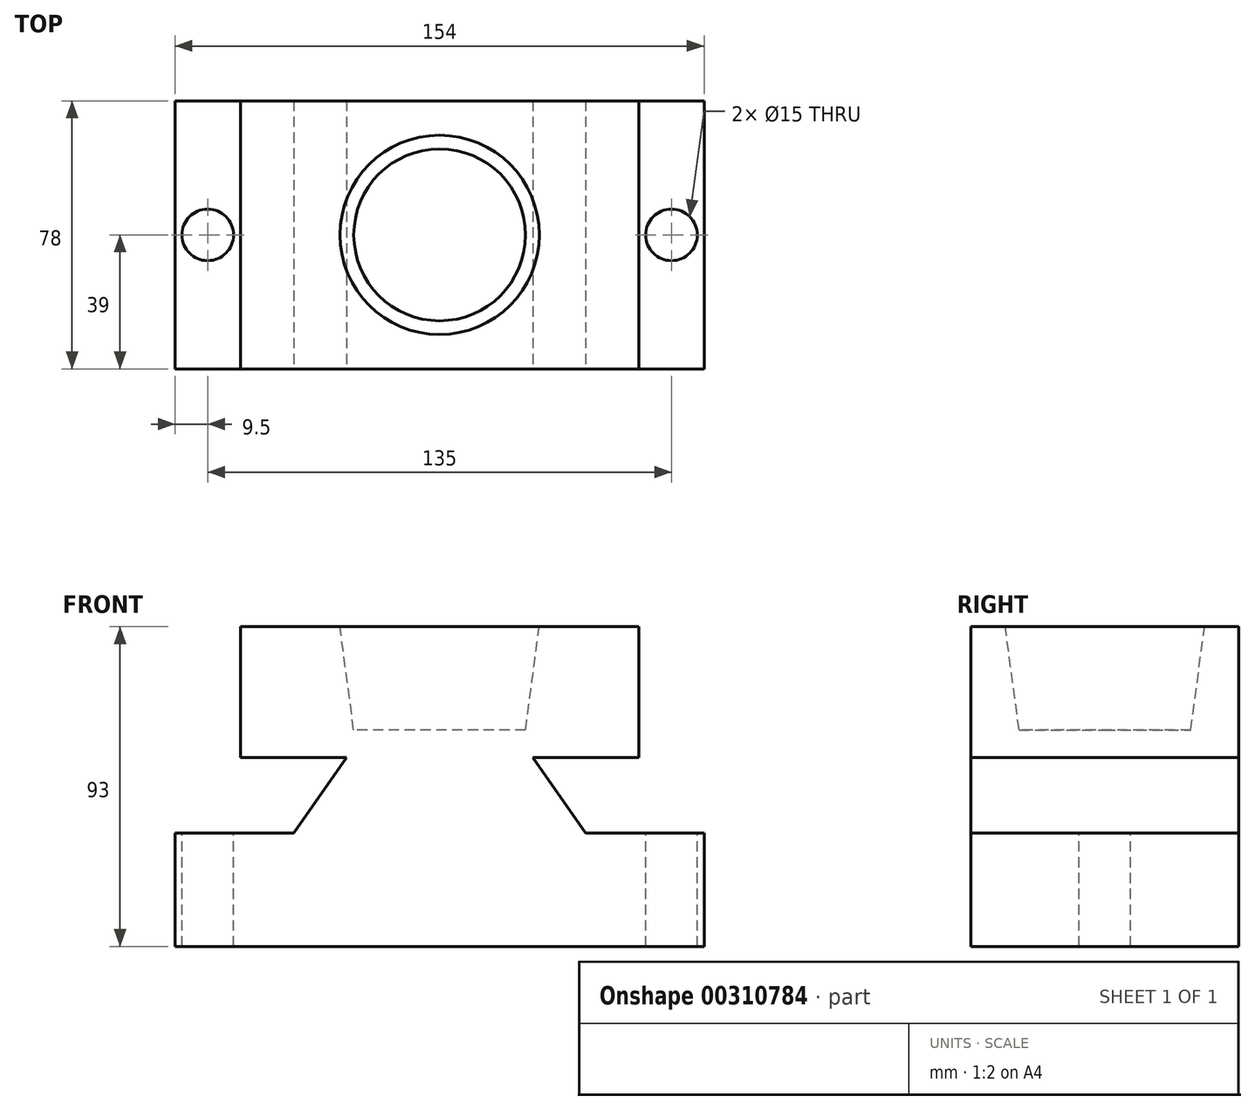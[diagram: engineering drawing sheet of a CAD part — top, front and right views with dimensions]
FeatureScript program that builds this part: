
annotation { "Feature Type Name" : "Feature", "Feature Type Description" : "" }
export const myFeature = defineFeature(function(context is Context, id is Id, definition is map)
    precondition{}
    {
        {
            var Q0;
            Q0=qCreatedBy(makeId("Top.planeOp"),FACE);
            var sketch = newSketch(context, id + "F0", { "sketchPlane" : qUnion([Q0])});
            skLineSegment(sketch, "E0.bottom", {"start": v(-77, 39) * mm, "end": v(77, 39) * mm});
            skLineSegment(sketch, "E0.top", {"start": v(-77, -39) * mm, "end": v(77, -39) * mm});
            skLineSegment(sketch, "E0.left", {"start": v(-77, 39) * mm, "end": v(-77, -39) * mm});
            skLineSegment(sketch, "E0.right", {"start": v(77, 39) * mm, "end": v(77, -39) * mm});
            skPoint(sketch, "E0.middle", {"position": v(0, 0) * mm});
            skSolve(sketch);
        }
        {
            var Q0;
            Q0=makeQuery(id+"F0.imprint","IMPRINT",FACE,{"disambiguationData":[TD([[makeQuery(id+"F0.imprint","IMPRINT",EDGE,{"derivedFrom":sQuery(id+"F0.wireOp",EDGE,"E0.bottom")}),-1.0]])]});
            extrude(context, id + "F1", {"entities" : qUnion([Q0]), "endBound" : BoundingType.SYMMETRIC, "depth" : 93 * mm});
        }
        {
            var Q0;
            Q0=makeQuery(id+"F1.opExtrude","SWEPT_FACE",FACE,{"disambiguationData":[OSD([sQuery(id+"F0.wireOp",EDGE,"E0.top")])]});
            var sketch = newSketch(context, id + "F2", { "sketchPlane" : qUnion([Q0])});
            skLineSegment(sketch, "E1", {"start": v(-77, -13.5) * mm, "end": v(-42.5, -13.5) * mm});
            skLineSegment(sketch, "E2", {"start": v(-42.5, -13.5) * mm, "end": v(-27.1, 8.5) * mm});
            skLineSegment(sketch, "E3", {"start": v(-27.1, 8.5) * mm, "end": v(-58, 8.5) * mm});
            skLineSegment(sketch, "E4", {"start": v(-58, 8.5) * mm, "end": v(-58, 46.5) * mm});
            skLineSegment(sketch, "E5", {"start": v(-58, 46.5) * mm, "end": v(58, 46.5) * mm});
            skLineSegment(sketch, "E6", {"start": v(58, 46.5) * mm, "end": v(58, 8.5) * mm});
            skLineSegment(sketch, "E7", {"start": v(58, 8.5) * mm, "end": v(27.1, 8.5) * mm});
            skLineSegment(sketch, "E8", {"start": v(27.1, 8.5) * mm, "end": v(42.5, -13.5) * mm});
            skLineSegment(sketch, "E9", {"start": v(42.5, -13.5) * mm, "end": v(77, -13.5) * mm});
            skSolve(sketch);
        }
        {
            var Q0;
            {var subQ5=sQuery(id+"F2.wireOp",EDGE,"E1");Q0=makeQuery(id+"F2.imprint","IMPRINT",FACE,{"disambiguationData":[TD([[makeQuery(id+"F2.imprint","IMPRINT",EDGE,{"derivedFrom":subQ5}),1.0]])]});}
            var Q1;
            {var subQ1=sQuery(id+"F2.wireOp",EDGE,"E6");Q1=makeQuery(id+"F2.imprint","IMPRINT",FACE,{"disambiguationData":[TD([[makeQuery(id+"F2.imprint","IMPRINT",EDGE,{"derivedFrom":subQ1}),1.0]])]});}
            extrude(context, id + "F3", {"entities" : qUnion([Q0, Q1]), "operationType" : NewBodyOperationType.REMOVE, "oppositeDirection" : true, "depth" : 80 * mm});
        }
        {
            var Q0;
            Q0=makeQuery(id+"F3.boolean.opBoolean","COPY",FACE,{"derivedFrom":makeQuery(id+"F3.opExtrude","SWEPT_FACE",FACE,{"disambiguationData":[OSD([sQuery(id+"F2.wireOp",EDGE,"E1")])]})});
            var sketch = newSketch(context, id + "F4", { "sketchPlane" : qUnion([Q0])});
            skCircle(sketch, "E10", {"center": v(-67.5, 0) * mm, "radius": 9.5 * mm});
            skCircle(sketch, "E11", {"center": v(-67.5, 0) * mm, "radius": 7.5 * mm});
            skSolve(sketch);
        }
        {
            var Q0;
            Q0=makeQuery(id+"F4.imprint","IMPRINT",FACE,{"disambiguationData":[TD([[makeQuery(id+"F4.imprint","IMPRINT",EDGE,{"derivedFrom":sQuery(id+"F4.wireOp",EDGE,"E11")}),1.0]])]});
            extrude(context, id + "F5", {"entities" : qUnion([Q0]), "operationType" : NewBodyOperationType.REMOVE, "oppositeDirection" : true, "depth" : 50 * mm});
        }
        {
            var Q0;
            Q0=makeQuery(id+"F1.opExtrude","CAP_FACE",FACE,{"disambiguationData":[OSD([sQuery(id+"F0.wireOp",EDGE,"E0.bottom"),sQuery(id+"F0.wireOp",EDGE,"E0.top"),sQuery(id+"F0.wireOp",EDGE,"E0.left"),sQuery(id+"F0.wireOp",EDGE,"E0.right")])],"isStart":false});
            var sketch = newSketch(context, id + "F6", { "sketchPlane" : qUnion([Q0])});
            skCircle(sketch, "E12", {"center": v(0, 0) * mm, "radius": 29 * mm});
            skCircle(sketch, "E13", {"center": v(0, 0) * mm, "radius": 31 * mm});
            skSolve(sketch);
        }
        {
            var Q0;
            Q0=makeQuery(id+"F6.imprint","IMPRINT",FACE,{"disambiguationData":[TD([[makeQuery(id+"F6.imprint","IMPRINT",EDGE,{"derivedFrom":sQuery(id+"F6.wireOp",EDGE,"E12")}),1.0]])]});
            extrude(context, id + "F7", {"entities" : qUnion([Q0]), "operationType" : NewBodyOperationType.REMOVE, "oppositeDirection" : true, "depth" : 30 * mm});
        }
        {
            var Q0;
            Q0=makeQuery(id+"F7.boolean.opBoolean","COPY",FACE,{"derivedFrom":makeQuery(id+"F7.opExtrude","CAP_FACE",FACE,{"disambiguationData":[OSD([sQuery(id+"F6.wireOp",EDGE,"E12")])],"isStart":false})});
            chamfer(context, id + "F8", {"entities" : qUnion([Q0]), "chamferType" : ChamferType.TWO_OFFSETS, "width1" : 4 * mm, "oppositeDirection" : false, "width2" : 30 * mm, "tangentPropagation" : true});
        }
        {
            var Q0;
            Q0=makeQuery(id+"F3.boolean.opBoolean","COPY",FACE,{"derivedFrom":makeQuery(id+"F3.opExtrude","SWEPT_FACE",FACE,{"disambiguationData":[OSD([sQuery(id+"F2.wireOp",EDGE,"E9")])]})});
            var sketch = newSketch(context, id + "F9", { "sketchPlane" : qUnion([Q0])});
            skCircle(sketch, "E14", {"center": v(67.5, 0) * mm, "radius": 9.5 * mm});
            skCircle(sketch, "E15", {"center": v(67.5, 0) * mm, "radius": 7.5 * mm});
            skSolve(sketch);
        }
        {
            var Q0;
            Q0=makeQuery(id+"F9.imprint","IMPRINT",FACE,{"disambiguationData":[TD([[makeQuery(id+"F9.imprint","IMPRINT",EDGE,{"derivedFrom":sQuery(id+"F9.wireOp",EDGE,"E15")}),1.0]])]});
            extrude(context, id + "F10", {"entities" : qUnion([Q0]), "operationType" : NewBodyOperationType.REMOVE, "oppositeDirection" : true, "depth" : 40 * mm});
        }
    });
